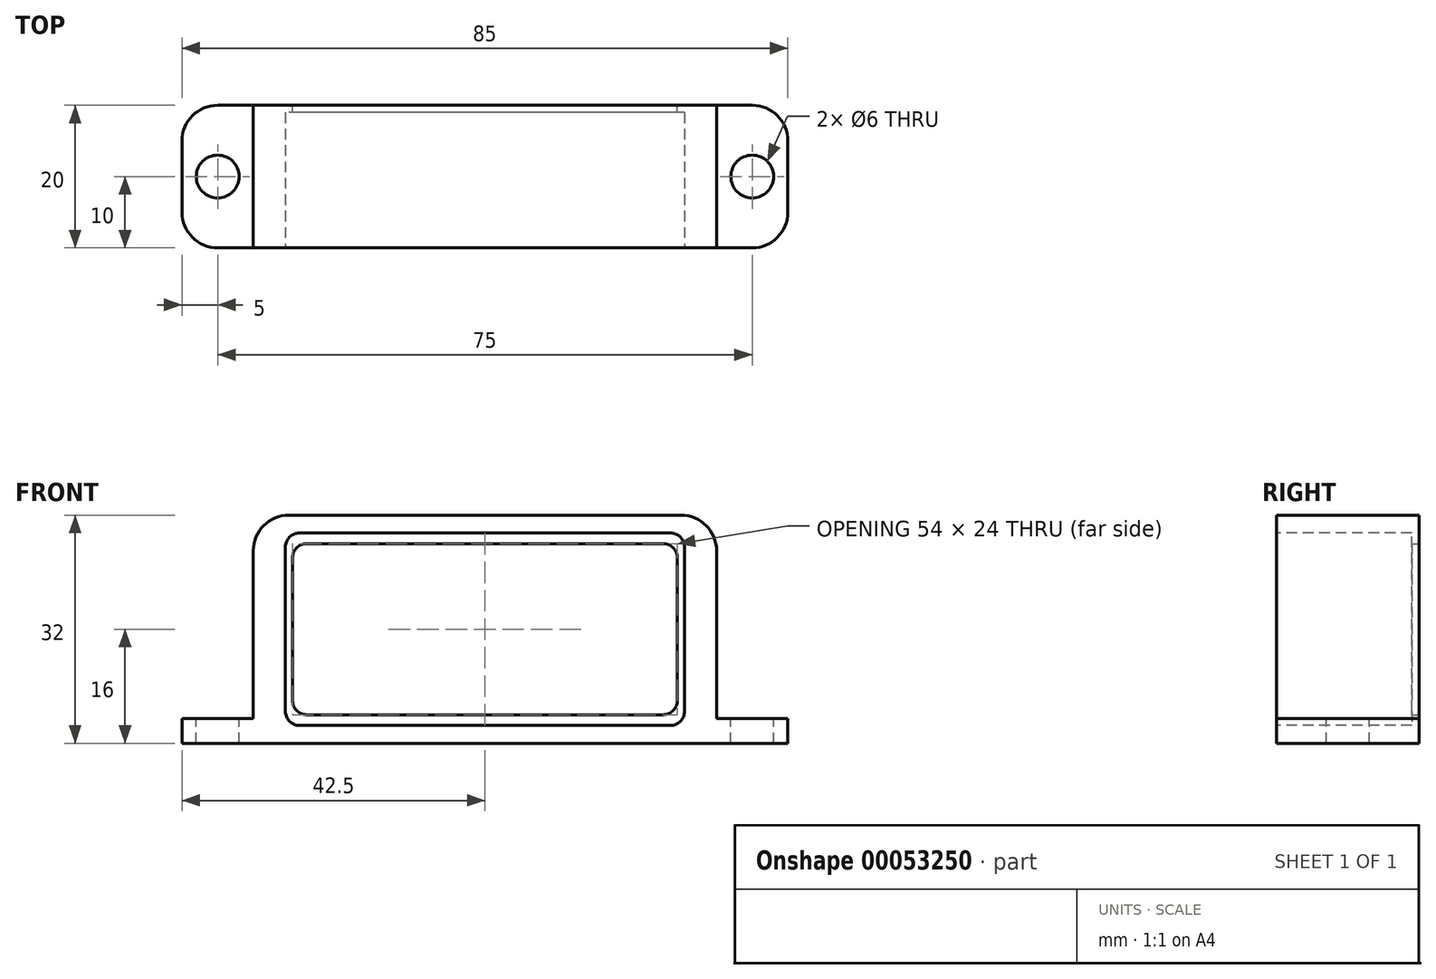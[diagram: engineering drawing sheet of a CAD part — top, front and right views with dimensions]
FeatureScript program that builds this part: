
annotation { "Feature Type Name" : "Feature", "Feature Type Description" : "" }
export const myFeature = defineFeature(function(context is Context, id is Id, definition is map)
    precondition{}
    {
        {
            var Q0;
            Q0=qCreatedBy(makeId("Front.planeOp"),FACE);
            var sketch = newSketch(context, id + "F0", { "sketchPlane" : qUnion([Q0])});
            skLineSegment(sketch, "E0.bottom", {"start": v(0, 0) * mm, "end": v(-65, 0) * mm});
            skLineSegment(sketch, "E0.top", {"start": v(0, 32) * mm, "end": v(-65, 32) * mm});
            skLineSegment(sketch, "E0.left", {"start": v(0, 0) * mm, "end": v(0, 32) * mm});
            skLineSegment(sketch, "E0.right", {"start": v(-65, 0) * mm, "end": v(-65, 32) * mm});
            skLineSegment(sketch, "E1.bottom", {"start": v(-65, 0) * mm, "end": v(-75, 0) * mm});
            skLineSegment(sketch, "E1.top", {"start": v(-65, 3.5) * mm, "end": v(-75, 3.5) * mm});
            skLineSegment(sketch, "E1.left", {"start": v(-65, 0) * mm, "end": v(-65, 3.5) * mm});
            skLineSegment(sketch, "E1.right", {"start": v(-75, 0) * mm, "end": v(-75, 3.5) * mm});
            skPoint(sketch, "E2.oppositeSnap0", {"position": v(-70, 3.5) * mm});
            skLineSegment(sketch, "E2.bottom", {"start": v(0, 0) * mm, "end": v(10, 0) * mm});
            skLineSegment(sketch, "E2.top", {"start": v(0, 3.5) * mm, "end": v(10, 3.5) * mm});
            skLineSegment(sketch, "E2.left", {"start": v(0, 0) * mm, "end": v(0, 3.5) * mm});
            skLineSegment(sketch, "E2.right", {"start": v(10, 0) * mm, "end": v(10, 3.5) * mm});
            skSolve(sketch);
        }
        {
            var Q0;
            Q0=makeQuery(id+"F0.imprint","IMPRINT",FACE,{"disambiguationData":[TD([[makeQuery(id+"F0.imprint","IMPRINT",EDGE,{"derivedFrom":sQuery(id+"F0.wireOp",EDGE,"E1.bottom")}),-1.0]])]});
            var Q1;
            Q1=makeQuery(id+"F0.imprint","IMPRINT",FACE,{"disambiguationData":[TD([[makeQuery(id+"F0.imprint","IMPRINT",EDGE,{"derivedFrom":sQuery(id+"F0.wireOp",EDGE,"E0.bottom")}),-1.0]])]});
            var Q2;
            Q2=makeQuery(id+"F0.imprint","IMPRINT",FACE,{"disambiguationData":[TD([[makeQuery(id+"F0.imprint","IMPRINT",EDGE,{"derivedFrom":sQuery(id+"F0.wireOp",EDGE,"E2.bottom")}),1.0]])]});
            extrude(context, id + "F1", {"entities" : qUnion([Q0, Q1, Q2]), "depth" : 20 * mm});
        }
        {
            var Q0;
            Q0=makeQuery(id+"F1.opExtrude","SWEPT_FACE",FACE,{"disambiguationData":[OSD([sQuery(id+"F0.wireOp",EDGE,"E2.top")])]});
            var sketch = newSketch(context, id + "F2", { "sketchPlane" : qUnion([Q0])});
            skLineSegment(sketch, "E3", {"start": v(0, -10) * mm, "end": v(10, -10) * mm, "construction": true});
            skCircle(sketch, "E4", {"center": v(5, -10) * mm, "radius": 3 * mm});
            skSolve(sketch);
        }
        {
            var Q0;
            Q0=makeQuery(id+"F2.imprint","IMPRINT",FACE,{"disambiguationData":[TD([[makeQuery(id+"F2.imprint","IMPRINT",EDGE,{"derivedFrom":sQuery(id+"F2.wireOp",EDGE,"E4")}),1.0]])]});
            extrude(context, id + "F3", {"entities" : qUnion([Q0]), "operationType" : NewBodyOperationType.REMOVE, "endBound" : BoundingType.THROUGH_ALL, "oppositeDirection" : true, "depth" : 25 * mm});
        }
        {
            var Q0;
            Q0=qCreatedBy(makeId("Right.planeOp"),FACE);
            cPlane(context, id + "F4", {"entities" : qUnion([Q0]), "cplaneType" : CPlaneType.OFFSET, "offset" : (65 / 2) * mm, "oppositeDirection" : true, "width" : 150 * mm, "height" : 150 * mm});
        }
        {
            var Q0;
            Q0=makeQuery(id+"F3.boolean.opBoolean","COPY",FACE,{"derivedFrom":makeQuery(id+"F3.opExtrude","SWEPT_FACE",FACE,{"disambiguationData":[OSD([sQuery(id+"F2.wireOp",EDGE,"E4")])]})});
            var Q1;
            Q1=qCreatedBy(id+"F4.planeOp",FACE);
            mirror(context, id + "F5", {"faces" : qUnion([Q0]), "mirrorPlane" : qUnion([Q1]), "patternType" : MirrorType.FACE});
        }
        {
            var Q0;
            Q0=makeQuery(id+"F1.opExtrude","SWEPT_EDGE",EDGE,{"disambiguationData":[OSD([sQuery(id+"F0.wireOp",EDGE,"E0.top"),sQuery(id+"F0.wireOp",EDGE,"E0.left")])]});
            var Q1;
            Q1=makeQuery(id+"F1.opExtrude","SWEPT_EDGE",EDGE,{"disambiguationData":[OSD([sQuery(id+"F0.wireOp",EDGE,"E0.top"),sQuery(id+"F0.wireOp",EDGE,"E0.right")])]});
            fillet(context, id + "F6", {"entities" : qUnion([Q0, Q1]), "radius" : 5 * mm, "tangentPropagation" : true, "allowEdgeOverflow" : false});
        }
        {
            var Q0;
            Q0=makeQuery(id+"F1.opExtrude","CAP_FACE",FACE,{"disambiguationData":[OSD([sQuery(id+"F0.wireOp",EDGE,"E0.bottom"),sQuery(id+"F0.wireOp",EDGE,"E0.top"),sQuery(id+"F0.wireOp",EDGE,"E0.left"),sQuery(id+"F0.wireOp",EDGE,"E0.right"),sQuery(id+"F0.wireOp",EDGE,"E1.bottom"),sQuery(id+"F0.wireOp",EDGE,"E1.top"),sQuery(id+"F0.wireOp",EDGE,"E1.right"),sQuery(id+"F0.wireOp",EDGE,"E2.bottom"),sQuery(id+"F0.wireOp",EDGE,"E2.top"),sQuery(id+"F0.wireOp",EDGE,"E2.right")])],"isStart":true});
            var sketch = newSketch(context, id + "F7", { "sketchPlane" : qUnion([Q0])});
            skLineSegment(sketch, "E5", {"start": v(32.5, 32) * mm, "end": v(32.5, 0) * mm, "construction": true});
            skLineSegment(sketch, "E6", {"start": v(32.5, 16) * mm, "end": v(10.72, 16) * mm, "construction": true});
            skLineSegment(sketch, "E7.rect.bottom", {"start": v(57.5, 4) * mm, "end": v(7.5, 4) * mm});
            skLineSegment(sketch, "E7.rect.top", {"start": v(57.5, 28) * mm, "end": v(7.5, 28) * mm});
            skLineSegment(sketch, "E7.rect.left", {"start": v(59.5, 6) * mm, "end": v(59.5, 26) * mm});
            skLineSegment(sketch, "E7.rect.right", {"start": v(5.5, 6) * mm, "end": v(5.5, 26) * mm});
            skPoint(sketch, "E7.rect.middle", {"position": v(32.5, 16) * mm});
            skPoint(sketch, "E8.visualSharp", {"position": v(5.5, 28) * mm});
            skArc(sketch, "E8.filletArc", {"start": v(7.5, 28) * mm, "mid": v(6.09, 27.41) * mm, "end": v(5.5, 26) * mm});
            skPoint(sketch, "E9.visualSharp", {"position": v(59.5, 28) * mm});
            skArc(sketch, "E9.filletArc", {"start": v(59.5, 26) * mm, "mid": v(58.91, 27.41) * mm, "end": v(57.5, 28) * mm});
            skPoint(sketch, "E10.visualSharp", {"position": v(59.5, 4) * mm});
            skArc(sketch, "E10.filletArc", {"start": v(57.5, 4) * mm, "mid": v(58.91, 4.59) * mm, "end": v(59.5, 6) * mm});
            skPoint(sketch, "E11.visualSharp", {"position": v(5.5, 4) * mm});
            skArc(sketch, "E11.filletArc", {"start": v(5.5, 6) * mm, "mid": v(6.09, 4.59) * mm, "end": v(7.5, 4) * mm});
            skSolve(sketch);
        }
        {
            var Q0;
            Q0=makeQuery(id+"F1.opExtrude","CAP_FACE",FACE,{"disambiguationData":[OSD([sQuery(id+"F0.wireOp",EDGE,"E0.bottom"),sQuery(id+"F0.wireOp",EDGE,"E0.top"),sQuery(id+"F0.wireOp",EDGE,"E0.left"),sQuery(id+"F0.wireOp",EDGE,"E0.right"),sQuery(id+"F0.wireOp",EDGE,"E1.bottom"),sQuery(id+"F0.wireOp",EDGE,"E1.top"),sQuery(id+"F0.wireOp",EDGE,"E1.right"),sQuery(id+"F0.wireOp",EDGE,"E2.bottom"),sQuery(id+"F0.wireOp",EDGE,"E2.top"),sQuery(id+"F0.wireOp",EDGE,"E2.right")])],"isStart":false});
            var sketch = newSketch(context, id + "F8", { "sketchPlane" : qUnion([Q0])});
            skLineSegment(sketch, "E12", {"start": v(-32.5, 32) * mm, "end": v(-32.5, 0) * mm, "construction": true});
            skLineSegment(sketch, "E13", {"start": v(-32.5, 16) * mm, "end": v(-44.81, 16) * mm, "construction": true});
            skPoint(sketch, "E13.endSnap0", {"position": v(-32.5, 16) * mm});
            skLineSegment(sketch, "E14.rect.bottom", {"start": v(-6.5, 2.5) * mm, "end": v(-58.5, 2.5) * mm});
            skLineSegment(sketch, "E14.rect.top", {"start": v(-6.5, 29.5) * mm, "end": v(-58.5, 29.5) * mm});
            skLineSegment(sketch, "E14.rect.left", {"start": v(-4.5, 4.5) * mm, "end": v(-4.5, 27.5) * mm});
            skLineSegment(sketch, "E14.rect.right", {"start": v(-60.5, 4.5) * mm, "end": v(-60.5, 27.5) * mm});
            skPoint(sketch, "E15.visualSharp", {"position": v(-60.5, 29.5) * mm});
            skArc(sketch, "E15.filletArc", {"start": v(-58.5, 29.5) * mm, "mid": v(-59.91, 28.91) * mm, "end": v(-60.5, 27.5) * mm});
            skPoint(sketch, "E16.visualSharp", {"position": v(-4.5, 29.5) * mm});
            skArc(sketch, "E16.filletArc", {"start": v(-4.5, 27.5) * mm, "mid": v(-5.09, 28.91) * mm, "end": v(-6.5, 29.5) * mm});
            skPoint(sketch, "E17.visualSharp", {"position": v(-4.5, 2.5) * mm});
            skArc(sketch, "E17.filletArc", {"start": v(-6.5, 2.5) * mm, "mid": v(-5.09, 3.09) * mm, "end": v(-4.5, 4.5) * mm});
            skPoint(sketch, "E18.visualSharp", {"position": v(-60.5, 2.5) * mm});
            skArc(sketch, "E18.filletArc", {"start": v(-60.5, 4.5) * mm, "mid": v(-59.91, 3.09) * mm, "end": v(-58.5, 2.5) * mm});
            skSolve(sketch);
        }
        {
            var Q0;
            Q0=makeQuery(id+"F8.imprint","IMPRINT",FACE,{"disambiguationData":[TD([[makeQuery(id+"F8.imprint","IMPRINT",EDGE,{"derivedFrom":sQuery(id+"F8.wireOp",EDGE,"E14.rect.bottom")}),-1.0]])]});
            extrude(context, id + "F9", {"entities" : qUnion([Q0]), "operationType" : NewBodyOperationType.REMOVE, "oppositeDirection" : true, "depth" : 19 * mm});
        }
        {
            var Q0;
            Q0=makeQuery(id+"F7.imprint","IMPRINT",FACE,{"disambiguationData":[TD([[makeQuery(id+"F7.imprint","IMPRINT",EDGE,{"derivedFrom":sQuery(id+"F7.wireOp",EDGE,"E7.rect.bottom")}),-1.0]])]});
            extrude(context, id + "F10", {"entities" : qUnion([Q0]), "operationType" : NewBodyOperationType.REMOVE, "oppositeDirection" : true, "depth" : 5 * mm});
        }
        {
            var Q0;
            Q0=makeQuery(id+"F1.opExtrude","CAP_EDGE",EDGE,{"disambiguationData":[OSD([sQuery(id+"F0.wireOp",EDGE,"E1.right")])],"isStart":false});
            var Q1;
            Q1=makeQuery(id+"F1.opExtrude","CAP_EDGE",EDGE,{"disambiguationData":[OSD([sQuery(id+"F0.wireOp",EDGE,"E1.right")])],"isStart":true});
            var Q2;
            Q2=makeQuery(id+"F1.opExtrude","CAP_EDGE",EDGE,{"disambiguationData":[OSD([sQuery(id+"F0.wireOp",EDGE,"E2.right")])],"isStart":false});
            var Q3;
            Q3=makeQuery(id+"F1.opExtrude","CAP_EDGE",EDGE,{"disambiguationData":[OSD([sQuery(id+"F0.wireOp",EDGE,"E2.right")])],"isStart":true});
            fillet(context, id + "F11", {"entities" : qUnion([Q0, Q1, Q2, Q3]), "radius" : 5 * mm, "tangentPropagation" : true, "allowEdgeOverflow" : false});
        }
    });
